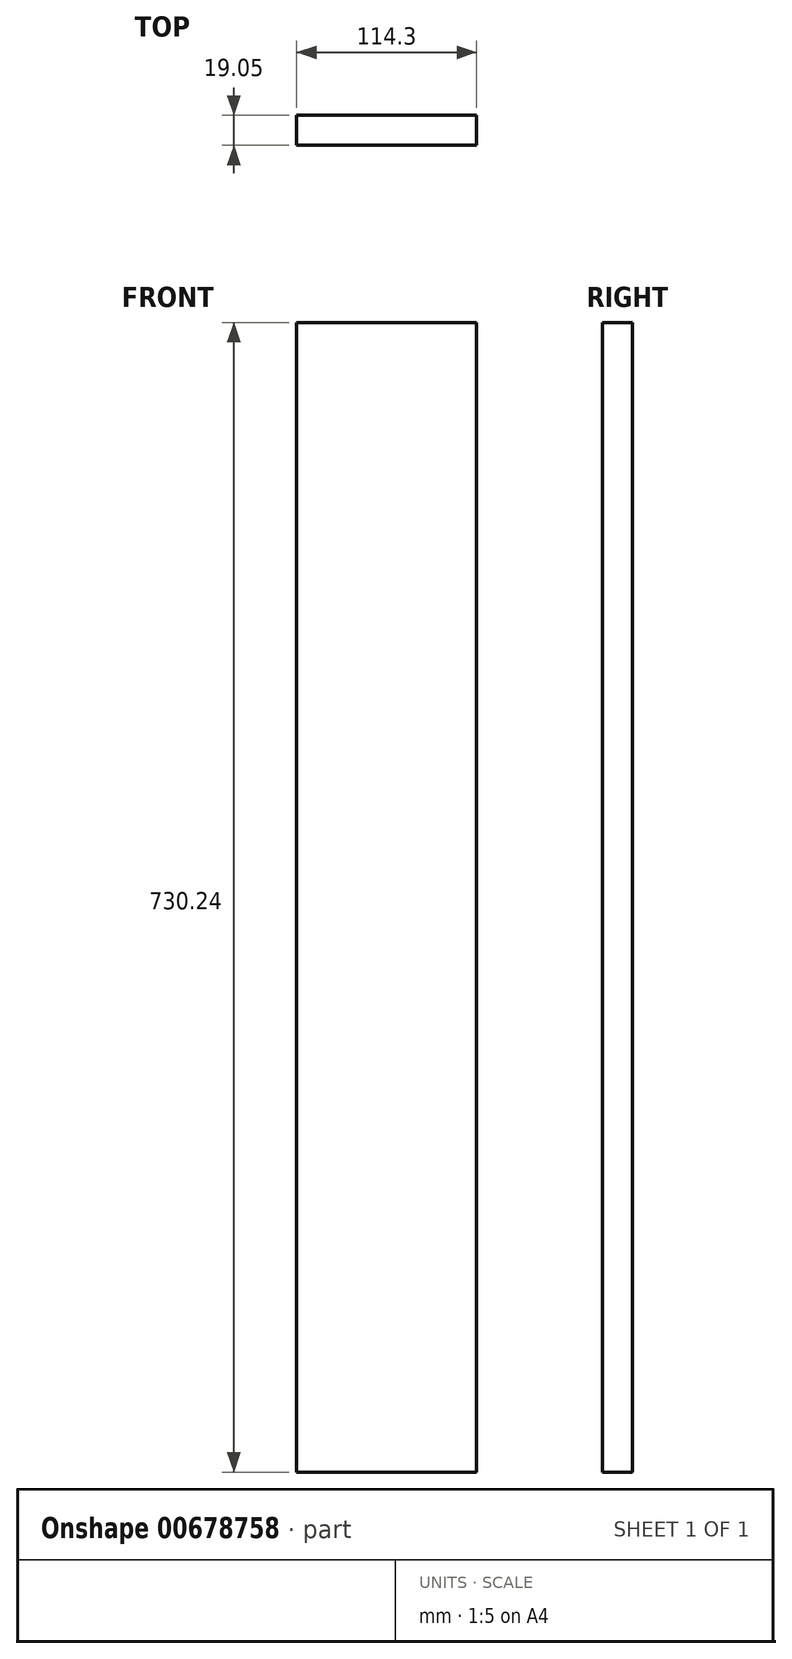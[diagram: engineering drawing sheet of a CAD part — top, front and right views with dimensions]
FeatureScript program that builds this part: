
annotation { "Feature Type Name" : "Feature", "Feature Type Description" : "" }
export const myFeature = defineFeature(function(context is Context, id is Id, definition is map)
    precondition{}
    {
        {
            var Q0;
            Q0=qCreatedBy(makeId("Front.planeOp"),FACE);
            var sketch = newSketch(context, id + "F0", { "sketchPlane" : qUnion([Q0])});
            skLineSegment(sketch, "E0.bottom", {"start": v(-57.15, 365.13) * mm, "end": v(57.15, 365.13) * mm});
            skLineSegment(sketch, "E0.top", {"start": v(-57.15, -365.12) * mm, "end": v(57.15, -365.12) * mm});
            skLineSegment(sketch, "E0.left", {"start": v(-57.15, 365.13) * mm, "end": v(-57.15, -365.12) * mm});
            skLineSegment(sketch, "E0.right", {"start": v(57.15, 365.13) * mm, "end": v(57.15, -365.12) * mm});
            skPoint(sketch, "E0.middle", {"position": v(0, 0) * mm});
            skSolve(sketch);
        }
        {
            var Q0;
            Q0=makeQuery(id+"F0.imprint","IMPRINT",FACE,{"disambiguationData":[TD([[makeQuery(id+"F0.imprint","IMPRINT",EDGE,{"derivedFrom":sQuery(id+"F0.wireOp",EDGE,"E0.bottom")}),-1.0]])]});
            extrude(context, id + "F1", {"entities" : qUnion([Q0]), "depth" : 19.05 * mm, "offsetDistance" : 25.4 * mm});
        }
    });
